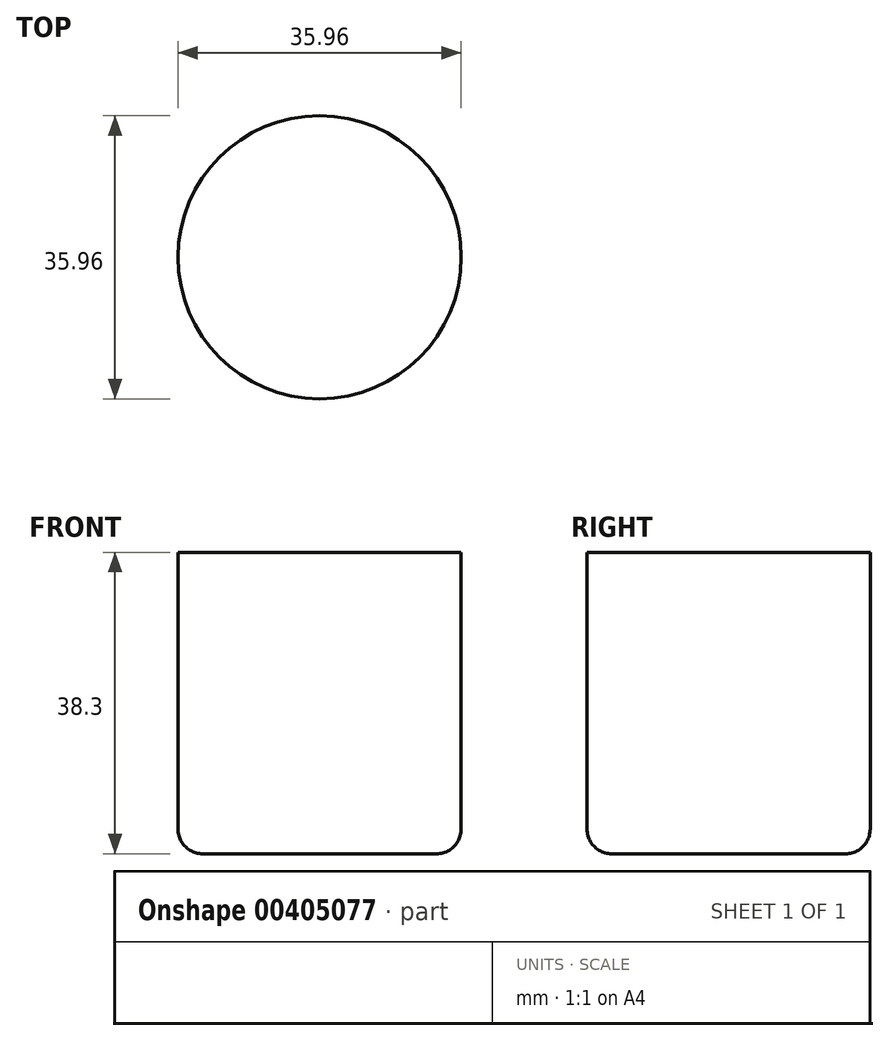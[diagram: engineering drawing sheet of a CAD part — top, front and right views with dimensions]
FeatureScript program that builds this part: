
annotation { "Feature Type Name" : "Feature", "Feature Type Description" : "" }
export const myFeature = defineFeature(function(context is Context, id is Id, definition is map)
    precondition{}
    {
        {
            var Q0;
            Q0=qCreatedBy(makeId("Front.planeOp"),FACE);
            var sketch = newSketch(context, id + "F0", { "sketchPlane" : qUnion([Q0])});
            skLineSegment(sketch, "E0", {"start": v(0, 0) * mm, "end": v(-15, 0) * mm});
            skLineSegment(sketch, "E1", {"start": v(-20, 5) * mm, "end": v(-20, 60) * mm});
            skLineSegment(sketch, "E2", {"start": v(0, -52.28) * mm, "end": v(0, 100.4) * mm, "construction": true});
            skPoint(sketch, "E3.visualSharp", {"position": v(-20, 0) * mm});
            skArc(sketch, "E3.filletArc", {"start": v(-20, 5) * mm, "mid": v(-18.54, 1.46) * mm, "end": v(-15, 0) * mm});
            skLineSegment(sketch, "E4", {"start": v(-20, 60) * mm, "end": v(-20.5, 60) * mm});
            skLineSegment(sketch, "E5", {"start": v(-21, 60.5) * mm, "end": v(-21, 60.5) * mm});
            skLineSegment(sketch, "E6", {"start": v(-20.5, 61) * mm, "end": v(-20, 61) * mm});
            skLineSegment(sketch, "E7.0", {"start": v(-18, 4) * mm, "end": v(-18, 60) * mm});
            skLineSegment(sketch, "E8.0", {"start": v(0, 2) * mm, "end": v(-16, 2) * mm});
            skPoint(sketch, "E9.visualSharp", {"position": v(-18, 2) * mm});
            skArc(sketch, "E9.filletArc", {"start": v(-18, 4) * mm, "mid": v(-17.41, 2.59) * mm, "end": v(-16, 2) * mm});
            skPoint(sketch, "E10.visualSharp", {"position": v(-21, 61) * mm});
            skArc(sketch, "E10.filletArc", {"start": v(-20.5, 61) * mm, "mid": v(-20.85, 60.85) * mm, "end": v(-21, 60.5) * mm});
            skPoint(sketch, "E11.visualSharp", {"position": v(-21, 60) * mm});
            skArc(sketch, "E11.filletArc", {"start": v(-21, 60.5) * mm, "mid": v(-20.85, 60.15) * mm, "end": v(-20.5, 60) * mm});
            skSolve(sketch);
        }
        {
            var Q0;
            Q0=sQuery(id+"F0.wireOp",EDGE,"E1");
            var Q1;
            Q1=sQuery(id+"F0.wireOp",EDGE,"E3.filletArc");
            var Q2;
            Q2=sQuery(id+"F0.wireOp",EDGE,"E4");
            var Q3;
            Q3=sQuery(id+"F0.wireOp",EDGE,"E11.filletArc");
            var Q4;
            Q4=sQuery(id+"F0.wireOp",EDGE,"E10.filletArc");
            var Q5;
            Q5=sQuery(id+"F0.wireOp",EDGE,"E6");
            var Q6;
            Q6=sQuery(id+"F0.wireOp",EDGE,"E2");
            revolve(context, id + "F1", {"bodyType" : ToolBodyType.SURFACE, "operationType" : NewBodyOperationType.INTERSECT, "surfaceEntities" : qUnion([Q0, Q1, Q2, Q3, Q4, Q5]), "axis" : qUnion([Q6]), "revolveType" : RevolveType.FULL});
        }
        {
            var Q0;
            Q0=qCreatedBy(makeId("Top.planeOp"),FACE);
            var sketch = newSketch(context, id + "F2", { "sketchPlane" : qUnion([Q0])});
            skCircle(sketch, "E12", {"center": v(0, 0) * mm, "radius": 17.98 * mm});
            skSolve(sketch);
        }
        {
            var Q0;
            Q0 = qSketchRegion(id + "F2", true);
            extrude(context, id + "F3", {"entities" : qUnion([Q0]), "depth" : 39 * mm, "hasSecondDirection" : true, "secondDirectionOppositeDirection" : false, "secondDirectionDepth" : 0.7 * mm});
        }
        {
            var Q0;
            Q0=makeQuery(id+"F3.opExtrude","CAP_FACE",FACE,{"disambiguationData":[OSD([sQuery(id+"F2.wireOp",EDGE,"E12")])],"isStart":true});
            fillet(context, id + "F4", {"entities" : qUnion([Q0]), "radius" : 3.14 * mm, "tangentPropagation" : true, "allowEdgeOverflow" : false});
        }
    });
